# Revit family: 1Electrical_Switchgear_Modelec_Confidence-Collection-double-vertical_FRA
name_source: partatom
category: Installations électriques
units: mm (PartAtom-declared; Revit-internal decimal feet)

## family parameters
Conserver l'orientation des annotations = Non
Cote de connecteur circulaire = Utiliser le diamètre
Couper avec des vides une fois chargée = Non
Hôte = Face
Numéro OmniClass = 23.80.50.11.14
Partagée = Non
Repere pour localisation dans la piece = Non
Titre OmniClass = Switches
Type d'élément = Normal

## types (1)
- Par défaut - veuillez charger le catalogue des types de familles Revit
    Apparent Load = 0 VA
    B1 = Non
    B1 Bas = Oui
    B1 Haut = Oui
    B2 = Non
    B2 Bas = Non
    B2 Haut = Non
    C1 = Non
    C3 Bas = Non
    Couleur du Mécanisme Bas = Modelec - Metal - Noir Mat
    Couleur du Mécanisme Centre = Modelec - Metal - Noir Mat
    Couleur du Mécanisme Haut = Modelec - Metal - Noir Mat
    Description = Les interrupteurs verticaux doubles de confiance et les plaques de couverture de prises en laiton, fabriquées en France, offrent un large éventail de fonctions : boutons poussoirs et bascules dans 4 finitions, avec ou sans LED, prises, prises Schuko, chargeurs USB, RJ45, HDMI, variateurs, volets roulants et bien plus encore. La collection Confiance est un grand classique du monde de la décoration. Ses formes épurées et le détail de ses finitions soignées en font un incontournable pour vos projets résidentiels, hôteliers ou tertiaires. La collection Confiance mérite son nom. La bonne touche, quel que soit votre choix esthétique. Disponible en 12 finitions.
    Description du Connecteur Bas = Interrupteur
    Description du Connecteur Centre = Interrupteur
    Description du Connecteur Haut = Interrupteur
    Elévation par défaut = 0 mm  [stored 0 ft]
    Fabricant = Modelec
    Installation instructions = https://www.modelec.com
    K1 Bas = Non
    K1 Haut = Non
    LED Centre = Non
    LEDs sur les Côtés = Non
    M1 Bas = Non
    M2 Bas = Non
    Modèle = Confidence Collection
    Number of Poles = 1
    P1 = Non
    P1 Bas = Non
    P1 Haut = Non
    P2 = Non
    P2 + LED = Non
    P2 Bas = Non
    P2 Haut = Non
    Power Factor = 1
    Product Documentation Link = https://www.modelec.com
    Product Page URL = https://www.modelec.com
    Product data url = https://bimobject.com
    Quantité 1 = 3
    Quantité 2 = 3
    Quantité 3 = 3
    Quantité 4 = 3
    Quantité 5 = 3
    R1 Bas = Non
    R1 Haut = Non
    U1 Bas = Non
    U1 Haut = Non
    URL = https://www.modelec.com
    Version = 1
    Voltage = 220 V
    Weight - Mass = 0.20 kg
    zEtreVisible = Oui
    zEtreVisibleCentre = Non
    zMasquage de la Région Visible Centre B = Oui
    zMasquage de la Région Visible à Droite Gauche B = Non
    zMasquage de la Région Visible à Droite LeftP = Non
    zMasquage du Centre Visible de la Région P = Non
    М1 Haut = Non
    М2 Haut = Non

note: [stored X ft] marks values corroborated as IEEE doubles in the binary element streams (Revit-internal decimal feet)

## geometry (parser evidence)
native form markers: Sweep x1
no freeform markers — native parametric forms only
